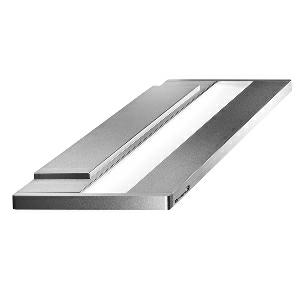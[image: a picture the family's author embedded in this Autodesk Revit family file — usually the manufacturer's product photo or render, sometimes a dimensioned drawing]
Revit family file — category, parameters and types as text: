
# Revit family: zera_bed_-_zew_9000_830_-_ul_00812992_3332
name_source: partatom
category: Lighting Fixtures
units: mm (PartAtom-declared; Revit-internal decimal feet)

## family parameters
Cut with Voids When Loaded = No
Host = Face
Light Source = No
Part Type = Normal
Room Calculation Point = No
Round Connector Dimension = Use Diameter
Shared = No

## types (1)
- AL+UL (1 x LED, 7600 lm, 4000K/3000K)
    Apparent Load = 76 VA
    Approval mark = CE
    CIE Flux Codes = 45 81 99 31 100
    Color Rendering = 90/80
    Color Temperature = 4000K/3000K
    Default Elevation = 2000 mm  [stored 6.56168 ft]
    Description = ZEW 9000/830|Wall-mounted luminaire|light source:   Warm white   |work equipment: Power supply unit|luminous flux: 8500 lm|light distribution: Direct/indirect|class of protection: I|technology: Switchable|mains lead: Connector 5 pin|glare control: Diffusor|special features: General light, indirect, 3000K, Ra80, DIN EN 60598-2-25, Reading light, direct, 2700K, Ra90, dir 4K 36W Ra95|
    Frequency = 50 Hz, 60 Hz
    Height = 20 mm  [stored 0.0656168 ft]
    Lamp = 1 x LED
    Lamp Light Flux = 7600 lm
    Lamp count = 1
    Length = 1050 mm
    Luminous efficacy = 100 lm/W
    Manufacturer = Waldmann
    ModVariant = No
    Model = 00812992
    Mounting Place = Wall
    Mounting Type = Surface mounted
    Number of Poles = 1
    OnlyDefault = Yes
    Power Factor = 1
    Product Name = ZERA.bed - ZEW 9000/830 - UL
    Product group = Wall mounted Luminaire
    ProductGroupID = 20
    Protection Class = Protection class I
    Protection Degree = IP 20
    RLX_Detail_Level = 1
    RLX_Emergency_Light_Flux = 0 lm
    RLX_Emergency_Type = 0
    RLX_Emergency_Type_DB = No
    RlxData = <blob elided: 62577 chars, md5=39fdc5d2>
    Socket = socket
    Standby Power = 0 W
    System Light Flux = 7600 lm
    System Power = 76 W
    Type Comments = General and Examation Light
    Type Image = zera_bed.jpg
    URL = http://relux.com
    VarID = al_ul_37f9
    Voltage = 230 V
    Voltage Range = 220-240 V
    Weight = 0.00 kg
    Width = 230 mm

note: [stored X ft] marks values corroborated as IEEE doubles in the binary element streams (Revit-internal decimal feet)

## geometry (parser evidence)
native form markers: Blend x4, Sweep x10
no freeform markers — native parametric forms only
